# Revit family: Legrand coffret XL³ 125
name_source: partatom
category: Equipement électrique
revit_build: Autodesk Revit 2018 (Build: 20170223_1515(x64)
units: mm (PartAtom-declared; Revit-internal decimal feet)

## family parameters
Basée sur le plan de construction = Oui
Configuration du panneau = Deux colonnes, circuits au sein
Cote de connecteur circulaire = Utiliser le diamètre
Couper avec des vides une fois chargée = Non
Numéro OmniClass = 23.80.30.11.17
Partagée = Non
Point de calcul de pièce = Non
Titre OmniClass = Distribution Boards and Control Panels
Toujours verticalement = Non
Type d'élément = Tableau de raccordement

## types (20) — shared parameters
Conditions Générale d'Utilisation = https://export.legrand.com
Couleur = RAL 9003
Elévation par défaut = 1219 mm
Fabricant = legrand
IK avec porte = 09
IK sans porte = 08
IP avec porte = 40
IP sans porte = 30
Largeur = 450 mm  [stored 1.47638 ft]
Matière = Polystyrène
Modèle = XL³ 125
URL = www.legrand.com

## per-type parameters (varying)
| type | 401611 | 401612 | 401613 | 401614 | 401631 | 401632 | 401633 | 401634 | 401641 | 401642 | 401643 | 401644 | 401646 | 401647 | 401648 | 401649 | 401656 | 401657 | 401658 | 401659 | Bornier N | Bornier T | Hauteur | profondeur |
| Coffret XL³ 125 401611 | Oui | Non | Non | Non | Non | Non | Non | Non | Non | Non | Non | Non | Non | Non | Non | Non | Non | Non | Non | Non |  | Bornier à connexion auto 5+18 trous Icc 10kA | 300 mm | 128 mm  [stored 0.419948 ft] |
| Coffret XL³ 125 401612 | Non | Oui | Non | Non | Non | Non | Non | Non | Non | Non | Non | Non | Non | Non | Non | Non | Non | Non | Non | Non |  | Bornier à connexion auto 5+27 trous Icc 10kA | 450 mm  [stored 1.47638 ft] | 128 mm  [stored 0.419948 ft] |
| Coffret XL³ 125 401613 | Non | Non | Oui | Non | Non | Non | Non | Non | Non | Non | Non | Non | Non | Non | Non | Non | Non | Non | Non | Non |  | Bornier à connexion auto 5+36 trous Icc 10kA | 600 mm | 125 mm  [stored 0.410105 ft] |
| Coffret XL³ 125 401614 | Non | Non | Non | Oui | Non | Non | Non | Non | Non | Non | Non | Non | Non | Non | Non | Non | Non | Non | Non | Non |  | Bornier à connexion auto 5+5+45 trous Icc 10kA | 750 mm  [stored 2.46063 ft] | 128 mm  [stored 0.419948 ft] |
| Coffret XL³ 125 401631 | Non | Non | Non | Non | Oui | Non | Non | Non | Non | Non | Non | Non | Non | Non | Non | Non | Non | Non | Non | Non |  | Bornier à connexion auto 5+18 trous Icc 10kA | 300 mm | 150 mm  [stored 0.492126 ft] |
| Coffret XL³ 125 401641 | Non | Non | Non | Non | Non | Non | Non | Non | Oui | Non | Non | Non | Non | Non | Non | Non | Non | Non | Non | Non |  | Bornier à connexion auto 5+18 trous Icc 10kA | 300 mm | 150 mm  [stored 0.492126 ft] |
| Coffret XL³ 125 401646 | Non | Non | Non | Non | Non | Non | Non | Non | Non | Non | Non | Non | Oui | Non | Non | Non | Non | Non | Non | Non | Bornier 2x8 trous | Bornier 17 trous | 300 mm | 150 mm  [stored 0.492126 ft] |
| Coffret XL³ 125 401656 | Non | Non | Non | Non | Non | Non | Non | Non | Non | Non | Non | Non | Non | Non | Non | Non | Oui | Non | Non | Non | Bornier 2x8 trous | Bornier 17 trous | 300 mm | 150 mm  [stored 0.492126 ft] |
| Coffret XL³ 125 401632 | Non | Non | Non | Non | Non | Oui | Non | Non | Non | Non | Non | Non | Non | Non | Non | Non | Non | Non | Non | Non |  | Bornier à connexion auto 5+27 trous Icc 10kA | 450 mm  [stored 1.47638 ft] | 150 mm  [stored 0.492126 ft] |
| Coffret XL³ 125 401642 | Non | Non | Non | Non | Non | Non | Non | Non | Non | Oui | Non | Non | Non | Non | Non | Non | Non | Non | Non | Non |  | Bornier à connexion auto 5+27 trous Icc 10kA | 450 mm  [stored 1.47638 ft] | 150 mm  [stored 0.492126 ft] |
| Coffret XL³ 125 401647 | Non | Non | Non | Non | Non | Non | Non | Non | Non | Non | Non | Non | Non | Oui | Non | Non | Non | Non | Non | Non | Bornier 3x8 trous | Bornier 22 trous | 450 mm  [stored 1.47638 ft] | 150 mm  [stored 0.492126 ft] |
| Coffret XL³ 125 401657 | Non | Non | Non | Non | Non | Non | Non | Non | Non | Non | Non | Non | Non | Non | Non | Non | Non | Oui | Non | Non | Bornier 3x8 trous | Bornier 22 trous | 450 mm  [stored 1.47638 ft] | 150 mm  [stored 0.492126 ft] |
| Coffret XL³ 125 401633 | Non | Non | Non | Non | Non | Non | Oui | Non | Non | Non | Non | Non | Non | Non | Non | Non | Non | Non | Non | Non |  | Bornier à connexion auto 5+36 trous Icc 10kA | 600 mm | 150 mm  [stored 0.492126 ft] |
| Coffret XL³ 125 401643 | Non | Non | Non | Non | Non | Non | Non | Non | Non | Non | Oui | Non | Non | Non | Non | Non | Non | Non | Non | Non |  | Bornier à connexion auto 5+36 trous Icc 10kA | 600 mm | 150 mm  [stored 0.492126 ft] |
| Coffret XL³ 125 401648 | Non | Non | Non | Non | Non | Non | Non | Non | Non | Non | Non | Non | Non | Non | Oui | Non | Non | Non | Non | Non | Bornier 4x8 trous | Bornier 27 trous | 600 mm | 150 mm  [stored 0.492126 ft] |
| Coffret XL³ 125 401658 | Non | Non | Non | Non | Non | Non | Non | Non | Non | Non | Non | Non | Non | Non | Non | Non | Non | Non | Oui | Non | Bornier 4x8 trous | Bornier 27 trous | 600 mm | 150 mm  [stored 0.492126 ft] |
| Coffret XL³ 125 401634 | Non | Non | Non | Non | Non | Non | Non | Oui | Non | Non | Non | Non | Non | Non | Non | Non | Non | Non | Non | Non |  | Bornier à connexion auto 5+5+45 trous Icc 10kA | 750 mm  [stored 2.46063 ft] | 150 mm  [stored 0.492126 ft] |
| Coffret XL³ 125 401644 | Non | Non | Non | Non | Non | Non | Non | Non | Non | Non | Non | Oui | Non | Non | Non | Non | Non | Non | Non | Non |  | Bornier à connexion auto 5+5+45 trous Icc 10kA | 750 mm  [stored 2.46063 ft] | 150 mm  [stored 0.492126 ft] |
| Coffret XL³ 125 401649 | Non | Non | Non | Non | Non | Non | Non | Non | Non | Non | Non | Non | Non | Non | Non | Oui | Non | Non | Non | Non | Bornier 5x8 trous | Bornier 35 trous | 750 mm  [stored 2.46063 ft] | 150 mm  [stored 0.492126 ft] |
| Coffret XL³ 125 401659 | Non | Non | Non | Non | Non | Non | Non | Non | Non | Non | Non | Non | Non | Non | Non | Non | Non | Non | Non | Oui | Bornier 5x8 trous | Bornier 35 trous | 750 mm  [stored 2.46063 ft] | 150 mm  [stored 0.492126 ft] |

note: [stored X ft] marks values corroborated as IEEE doubles in the binary element streams (Revit-internal decimal feet)
